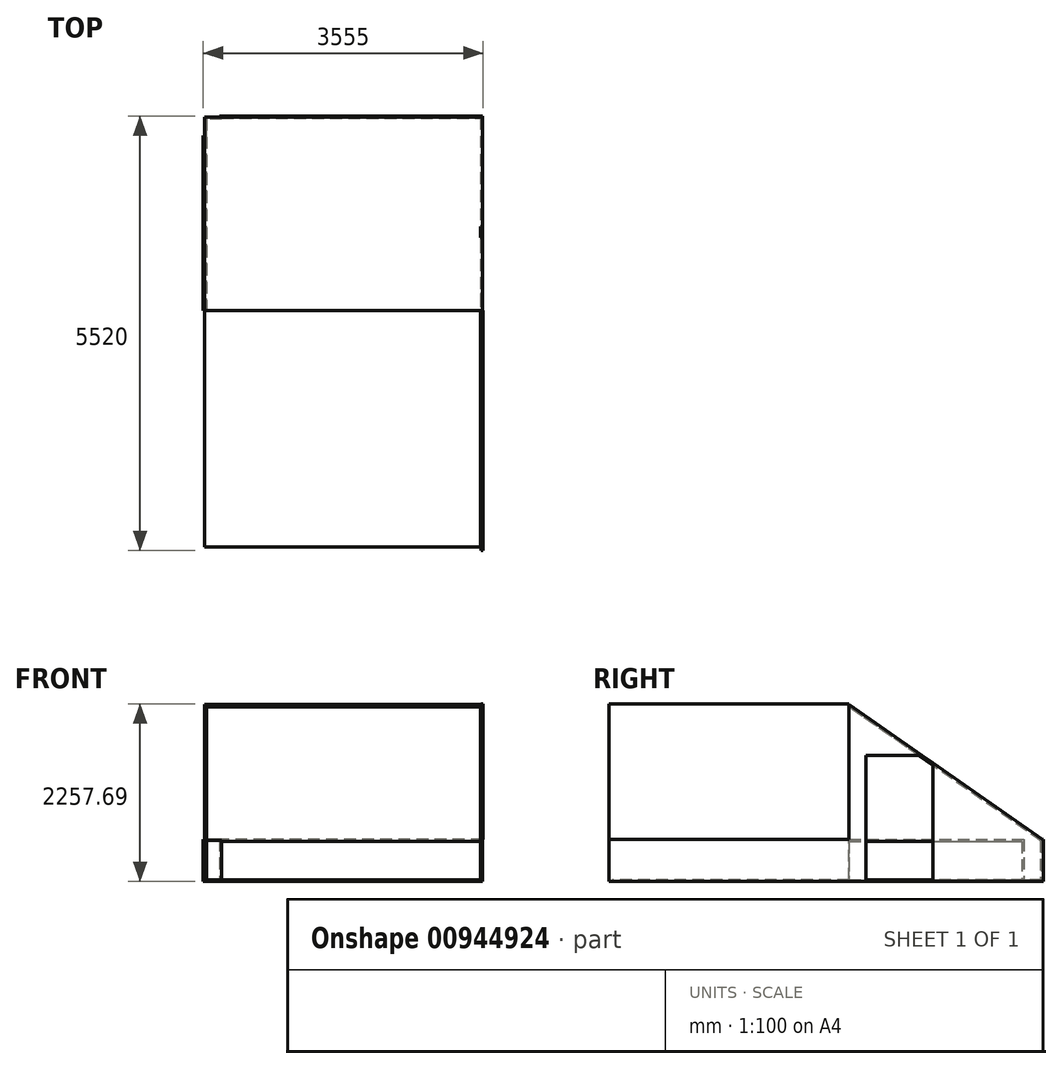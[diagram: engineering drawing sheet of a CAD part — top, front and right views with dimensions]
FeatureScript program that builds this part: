
annotation { "Feature Type Name" : "Feature", "Feature Type Description" : "" }
export const myFeature = defineFeature(function(context is Context, id is Id, definition is map)
    precondition{}
    {
        {
            var Q0;
            Q0=qCreatedBy(makeId("Top.planeOp"),FACE);
            var sketch = newSketch(context, id + "F0", { "sketchPlane" : qUnion([Q0])});
            skLineSegment(sketch, "E0", {"start": v(0, 0) * mm, "end": v(0, 2200) * mm});
            skLineSegment(sketch, "E1", {"start": v(0, 2200) * mm, "end": v(210, 2200) * mm});
            skLineSegment(sketch, "E2", {"start": v(210, 2200) * mm, "end": v(210, 2450) * mm});
            skLineSegment(sketch, "E3", {"start": v(210, 2450) * mm, "end": v(3510, 2450) * mm});
            skLineSegment(sketch, "E4", {"start": v(3510, 2450) * mm, "end": v(3510, -3050) * mm});
            skLineSegment(sketch, "E5.0", {"start": v(3530, 2470) * mm, "end": v(3530, -3050) * mm});
            skLineSegment(sketch, "E5.1", {"start": v(-20, 0) * mm, "end": v(-20, 2220) * mm});
            skLineSegment(sketch, "E5.2", {"start": v(-20, 2220) * mm, "end": v(190, 2220) * mm});
            skLineSegment(sketch, "E5.3", {"start": v(190, 2220) * mm, "end": v(190, 2470) * mm});
            skLineSegment(sketch, "E5.4", {"start": v(190, 2470) * mm, "end": v(3530, 2470) * mm});
            skLineSegment(sketch, "E6", {"start": v(0, 0) * mm, "end": v(-20, 0) * mm});
            skLineSegment(sketch, "E7", {"start": v(3510, -3050) * mm, "end": v(3530, -3050) * mm});
            skSolve(sketch);
        }
        {
            var Q0;
            Q0 = qSketchRegion(id + "F0", true);
            extrude(context, id + "F1", {"entities" : qUnion([Q0]), "depth" : 535 * mm, "offsetDistance" : 25 * mm});
        }
        {
            var Q0;
            Q0=makeQuery(id+"F1.opExtrude","SWEPT_FACE",FACE,{"disambiguationData":[OSD([sQuery(id+"F0.wireOp",EDGE,"E0")])]});
            var sketch = newSketch(context, id + "F2", { "sketchPlane" : qUnion([Q0])});
            skLineSegment(sketch, "E8", {"start": v(2200, 0) * mm, "end": v(2457.42, 0) * mm, "construction": true});
            skLineSegment(sketch, "E9", {"start": v(2457.42, 0) * mm, "end": v(2457.42, 535) * mm, "construction": true});
            skLineSegment(sketch, "E10", {"start": v(2457.42, 535) * mm, "end": v(0, 2249.34) * mm, "construction": true});
            skLineSegment(sketch, "E11", {"start": v(0, 2249.34) * mm, "end": v(0, 0) * mm, "construction": true});
            skLineSegment(sketch, "E12", {"start": v(357.42, 0) * mm, "end": v(357.42, 2000) * mm, "construction": true});
            skLineSegment(sketch, "E13", {"start": v(0, 0) * mm, "end": v(0, 2249.34) * mm});
            skLineSegment(sketch, "E14", {"start": v(2457.42, 535) * mm, "end": v(2457.42, 0) * mm});
            skLineSegment(sketch, "E15", {"start": v(0, 0) * mm, "end": v(2457.42, 0) * mm});
            skLineSegment(sketch, "E16", {"start": v(2457.42, 0) * mm, "end": v(2457.42, 535) * mm});
            skLineSegment(sketch, "E17", {"start": v(2457.42, 535) * mm, "end": v(0, 2249.34) * mm});
            skSolve(sketch);
        }
        {
            var Q0;
            Q0 = qSketchRegion(id + "F2", true);
            extrude(context, id + "F3", {"entities" : qUnion([Q0]), "operationType" : NewBodyOperationType.ADD, "depth" : 3530 * mm, "offsetDistance" : 25 * mm});
        }
        {
            var Q0;
            Q0=makeQuery(id+"F3.boolean.opBoolean","MERGE",FACE,{"derivedFrom":[makeQuery(id+"F1.opExtrude","SWEPT_FACE",FACE,{"disambiguationData":[OSD([sQuery(id+"F0.wireOp",EDGE,"E6")])]}),makeQuery(id+"F3.opExtrude","SWEPT_FACE",FACE,{"disambiguationData":[OSD([sQuery(id+"F2.wireOp",EDGE,"E13")])]})]});
            shell(context, id + "F4", {"entities" : qUnion([Q0]), "thickness" : 25 * mm});
        }
        {
            var Q0;
            Q0=makeQuery(id+"F1.opExtrude","SWEPT_FACE",FACE,{"disambiguationData":[OSD([sQuery(id+"F0.wireOp",EDGE,"E4")])]});
            var sketch = newSketch(context, id + "F5", { "sketchPlane" : qUnion([Q0])});
            skLineSegment(sketch, "E18.bottom", {"start": v(3050, 535) * mm, "end": v(0, 535) * mm});
            skLineSegment(sketch, "E18.top", {"start": v(3050, 2257.69) * mm, "end": v(0, 2257.69) * mm});
            skLineSegment(sketch, "E18.left", {"start": v(3050, 535) * mm, "end": v(3050, 2257.69) * mm});
            skLineSegment(sketch, "E18.right", {"start": v(0, 535) * mm, "end": v(0, 2257.69) * mm});
            skSolve(sketch);
        }
        {
            var Q0;
            Q0 = qSketchRegion(id + "F5", true);
            extrude(context, id + "F6", {"entities" : qUnion([Q0]), "operationType" : NewBodyOperationType.ADD, "oppositeDirection" : true, "depth" : 25 * mm, "offsetDistance" : 25 * mm});
        }
        {
            var Q0;
            Q0=makeQuery(id+"F4.opShell","OFFSET_FACE",FACE,{"disambiguationData":[OSD([sQuery(id+"F0.wireOp",EDGE,"E5.0"),sQuery(id+"F2.wireOp",EDGE,"E13"),sQuery(id+"F2.wireOp",EDGE,"E15"),sQuery(id+"F2.wireOp",EDGE,"E16"),sQuery(id+"F2.wireOp",EDGE,"E17")])]});
            var sketch = newSketch(context, id + "F7", { "sketchPlane" : qUnion([Q0])});
            skLineSegment(sketch, "E19.bottom", {"start": v(-1065, 25) * mm, "end": v(-215, 25) * mm});
            skLineSegment(sketch, "E19.top", {"start": v(-1065, 1605) * mm, "end": v(-215, 1605) * mm});
            skLineSegment(sketch, "E19.left", {"start": v(-1065, 25) * mm, "end": v(-1065, 1605) * mm});
            skLineSegment(sketch, "E19.right", {"start": v(-215, 25) * mm, "end": v(-215, 1605) * mm});
            skSolve(sketch);
        }
        {
            var Q0;
            Q0 = qSketchRegion(id + "F7", true);
            extrude(context, id + "F8", {"entities" : qUnion([Q0]), "operationType" : NewBodyOperationType.REMOVE, "oppositeDirection" : true, "depth" : 25 * mm, "offsetDistance" : 25 * mm});
        }
        {
            var Q0;
            Q0=makeQuery(id+"F8.boolean.opBoolean","MERGE",FACE,{"derivedFrom":[makeQuery(id+"F4.opShell","OFFSET_FACE",FACE,{"disambiguationData":[OSD([sQuery(id+"F0.wireOp",EDGE,"E0"),sQuery(id+"F0.wireOp",EDGE,"E1"),sQuery(id+"F0.wireOp",EDGE,"E2"),sQuery(id+"F0.wireOp",EDGE,"E3"),sQuery(id+"F0.wireOp",EDGE,"E4"),sQuery(id+"F0.wireOp",EDGE,"E5.0"),sQuery(id+"F0.wireOp",EDGE,"E5.1"),sQuery(id+"F0.wireOp",EDGE,"E5.2"),sQuery(id+"F0.wireOp",EDGE,"E5.3"),sQuery(id+"F0.wireOp",EDGE,"E5.4"),sQuery(id+"F0.wireOp",EDGE,"E6"),sQuery(id+"F0.wireOp",EDGE,"E7"),sQuery(id+"F2.wireOp",EDGE,"E15")])]})],"fromTools":[makeQuery(id+"F8.opExtrude","SWEPT_FACE",FACE,{"disambiguationData":[OSD([sQuery(id+"F7.wireOp",EDGE,"E19.bottom")])]})]});
            var sketch = newSketch(context, id + "F9", { "sketchPlane" : qUnion([Q0])});
            skLineSegment(sketch, "E20.bottom", {"start": v(3505, 0) * mm, "end": v(0, 0) * mm});
            skLineSegment(sketch, "E20.top", {"start": v(3505, -3008.03) * mm, "end": v(0, -3008.03) * mm});
            skLineSegment(sketch, "E20.left", {"start": v(3505, 0) * mm, "end": v(3505, -3008.03) * mm});
            skLineSegment(sketch, "E20.right", {"start": v(0, 0) * mm, "end": v(0, -3008.03) * mm});
            skSolve(sketch);
        }
        {
            var Q0;
            Q0 = qSketchRegion(id + "F9", true);
            extrude(context, id + "F10", {"entities" : qUnion([Q0]), "operationType" : NewBodyOperationType.ADD, "oppositeDirection" : true, "depth" : 25 * mm, "offsetDistance" : 25 * mm});
        }
    });
